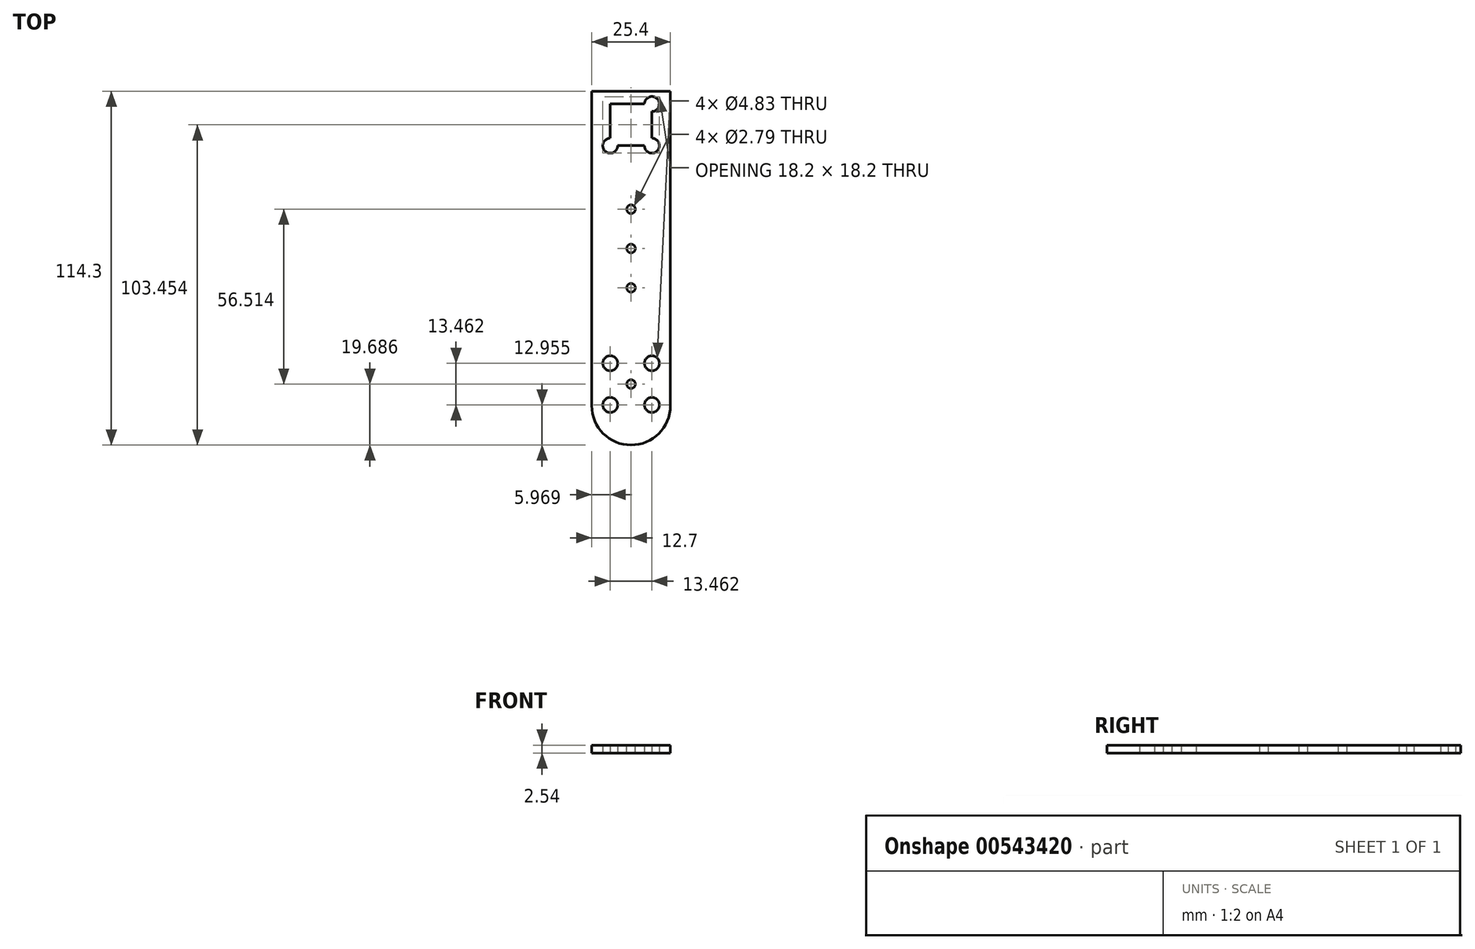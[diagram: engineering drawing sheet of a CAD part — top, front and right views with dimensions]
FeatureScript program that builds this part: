
annotation { "Feature Type Name" : "Feature", "Feature Type Description" : "" }
export const myFeature = defineFeature(function(context is Context, id is Id, definition is map)
    precondition{}
    {
        {
            var Q0;
            Q0=qCreatedBy(makeId("Top.planeOp"),FACE);
            var sketch = newSketch(context, id + "F0", { "sketchPlane" : qUnion([Q0])});
            skLineSegment(sketch, "E0.left", {"start": v(12.7, 50.8) * mm, "end": v(12.7, -50.8) * mm});
            skLineSegment(sketch, "E0.right", {"start": v(-12.7, 50.8) * mm, "end": v(-12.7, -50.8) * mm});
            skPoint(sketch, "E0.middle", {"position": v(0, 0) * mm});
            skLineSegment(sketch, "E1.bottom", {"start": v(6.73, -50.55) * mm, "end": v(-6.73, -50.55) * mm});
            skLineSegment(sketch, "E1.top", {"start": v(6.73, -37.08) * mm, "end": v(-6.73, -37.08) * mm});
            skLineSegment(sketch, "E1.left", {"start": v(6.73, -50.55) * mm, "end": v(6.73, -37.08) * mm});
            skLineSegment(sketch, "E1.right", {"start": v(-6.73, -50.55) * mm, "end": v(-6.73, -37.08) * mm});
            skPoint(sketch, "E1.middle", {"position": v(0, -43.81) * mm});
            skCircle(sketch, "E2", {"center": v(-6.73, -37.08) * mm, "radius": 2.41 * mm});
            skCircle(sketch, "E3", {"center": v(6.73, -37.08) * mm, "radius": 2.41 * mm});
            skCircle(sketch, "E4", {"center": v(6.73, -50.55) * mm, "radius": 2.41 * mm});
            skCircle(sketch, "E5", {"center": v(-6.73, -50.55) * mm, "radius": 2.41 * mm});
            skArc(sketch, "E6", {"start": v(-12.7, -50.8) * mm, "mid": v(0, -63.5) * mm, "end": v(12.7, -50.8) * mm});
            skLineSegment(sketch, "E7", {"start": v(-12.7, 50.8) * mm, "end": v(12.7, 50.8) * mm});
            skLineSegment(sketch, "E8", {"start": v(-12.7, -1.93) * mm, "end": v(12.7, -1.93) * mm});
            skLineSegment(sketch, "E9.MirrorCS", {"start": v(6.73, 33.22) * mm, "end": v(-6.73, 33.22) * mm});
            skLineSegment(sketch, "E10.MirrorCS", {"start": v(6.73, 46.69) * mm, "end": v(-6.73, 46.69) * mm});
            skCircle(sketch, "E11.MirrorC", {"center": v(-6.73, 46.69) * mm, "radius": 2.41 * mm});
            skCircle(sketch, "E12.MirrorC", {"center": v(-6.73, 33.22) * mm, "radius": 2.41 * mm});
            skLineSegment(sketch, "E13.MirrorCS", {"start": v(6.73, 46.69) * mm, "end": v(6.73, 33.22) * mm});
            skLineSegment(sketch, "E14.MirrorCS", {"start": v(-6.73, 46.69) * mm, "end": v(-6.73, 33.22) * mm});
            skPoint(sketch, "E15.MirrorP", {"position": v(0, 39.95) * mm});
            skCircle(sketch, "E16.MirrorC", {"center": v(6.73, 46.69) * mm, "radius": 2.41 * mm});
            skCircle(sketch, "E17.MirrorC", {"center": v(6.73, 33.22) * mm, "radius": 2.41 * mm});
            skSolve(sketch);
        }
        {
            var Q0;
            Q0=qSketchRegion(id+"F0",true);
            var Q1;
            {var subQ5=sQuery(id+"F0.wireOp",EDGE,"E4");var subQ10=sQuery(id+"F0.wireOp",EDGE,"E1.bottom");var subQ15=makeQuery(id+"F0.imprint","INTERSECT",VERTEX,{"derivedFrom":[subQ10,subQ5]});Q1=makeQuery(id+"F0.imprint","IMPRINT",FACE,{"disambiguationData":[TD([[makeQuery(id+"F0.imprint","IMPRINT",EDGE,{"disambiguationData":[TD([[subQ15,-1.0]])],"derivedFrom":subQ10}),-1.0]])]});}
            var Q2;
            {var subQ0=sQuery(id+"F0.wireOp",EDGE,"E10.MirrorCS");var subQ1=sQuery(id+"F0.wireOp",EDGE,"E11.MirrorC");var subQ2=makeQuery(id+"F0.imprint","INTERSECT",VERTEX,{"derivedFrom":[subQ1,subQ0]});Q2=makeQuery(id+"F0.imprint","IMPRINT",FACE,{"disambiguationData":[TD([[makeQuery(id+"F0.imprint","IMPRINT",EDGE,{"disambiguationData":[TD([[subQ2,-1.0]])],"derivedFrom":subQ1}),1.0]])]});}
            extrude(context, id + "F1", {"entities" : qUnion([Q0, Q1, Q2]), "depth" : 2.54 * mm, "offsetDistance" : 25.4 * mm});
        }
        {
            var Q0;
            Q0=makeQuery(id+"F1.opExtrude","CAP_FACE",FACE,{"disambiguationData":[OSD([sQuery(id+"F0.wireOp",EDGE,"E0.left"),sQuery(id+"F0.wireOp",EDGE,"E0.right"),sQuery(id+"F0.wireOp",EDGE,"E2"),sQuery(id+"F0.wireOp",EDGE,"E3"),sQuery(id+"F0.wireOp",EDGE,"E4"),sQuery(id+"F0.wireOp",EDGE,"E5"),sQuery(id+"F0.wireOp",EDGE,"E6"),sQuery(id+"F0.wireOp",EDGE,"t0C233Ww-Tjgr-lEmG-p7Nm-2mTDBtev8aHC")])],"isStart":false});
            var sketch = newSketch(context, id + "F2", { "sketchPlane" : qUnion([Q0])});
            skCircle(sketch, "E18", {"center": v(0, 0) * mm, "radius": 1.4 * mm});
            skLineSegment(sketch, "E19", {"start": v(-6.73, -37.08) * mm, "end": v(6.73, -50.55) * mm});
            skLineSegment(sketch, "E20", {"start": v(6.73, -37.08) * mm, "end": v(-6.73, -50.55) * mm});
            skCircle(sketch, "E21", {"center": v(0, -43.81) * mm, "radius": 1.4 * mm});
            skLineSegment(sketch, "E22", {"start": v(-8.4, 0) * mm, "end": v(10, 0) * mm});
            skCircle(sketch, "E23.MirrorC", {"center": v(0, 43.81) * mm, "radius": 1.4 * mm});
            skSolve(sketch);
        }
        {
            var Q0;
            Q0=qSketchRegion(id+"F2",true);
            extrude(context, id + "F3", {"entities" : qUnion([Q0]), "operationType" : NewBodyOperationType.REMOVE, "endBound" : BoundingType.THROUGH_ALL, "oppositeDirection" : true, "depth" : 6.35 * mm, "offsetDistance" : 25.4 * mm});
        }
        {
            var Q0;
            Q0=makeQuery(id+"F1.opExtrude","CAP_FACE",FACE,{"disambiguationData":[OSD([sQuery(id+"F0.wireOp",EDGE,"E0.left"),sQuery(id+"F0.wireOp",EDGE,"E0.right"),sQuery(id+"F0.wireOp",EDGE,"E2"),sQuery(id+"F0.wireOp",EDGE,"E3"),sQuery(id+"F0.wireOp",EDGE,"E4"),sQuery(id+"F0.wireOp",EDGE,"E5"),sQuery(id+"F0.wireOp",EDGE,"E6"),sQuery(id+"F0.wireOp",EDGE,"E7"),sQuery(id+"F0.wireOp",EDGE,"E11.MirrorC"),sQuery(id+"F0.wireOp",EDGE,"E12.MirrorC"),sQuery(id+"F0.wireOp",EDGE,"E16.MirrorC"),sQuery(id+"F0.wireOp",EDGE,"E17.MirrorC")])],"isStart":false});
            var sketch = newSketch(context, id + "F4", { "sketchPlane" : qUnion([Q0])});
            skLineSegment(sketch, "E24", {"start": v(0, 13.88) * mm, "end": v(0, -13.79) * mm});
            skCircle(sketch, "E25", {"center": v(0, 12.7) * mm, "radius": 1.4 * mm});
            skCircle(sketch, "E26", {"center": v(0, -12.7) * mm, "radius": 1.4 * mm});
            skPoint(sketch, "E27", {"position": v(0, 0) * mm});
            skSolve(sketch);
        }
        {
            var Q0;
            Q0=makeQuery(id+"F4.imprint","IMPRINT",FACE,{"disambiguationData":[TD([[makeQuery(id+"F4.imprint","IMPRINT",EDGE,{"derivedFrom":sQuery(id+"F4.wireOp",EDGE,"E25")}),1.0]])]});
            var Q1;
            Q1=makeQuery(id+"F4.imprint","IMPRINT",FACE,{"disambiguationData":[TD([[makeQuery(id+"F4.imprint","IMPRINT",EDGE,{"derivedFrom":sQuery(id+"F4.wireOp",EDGE,"E26")}),1.0]])]});
            extrude(context, id + "F5", {"entities" : qUnion([Q0, Q1]), "operationType" : NewBodyOperationType.REMOVE, "oppositeDirection" : true, "depth" : 25.4 * mm, "offsetDistance" : 25.4 * mm});
        }
    });
